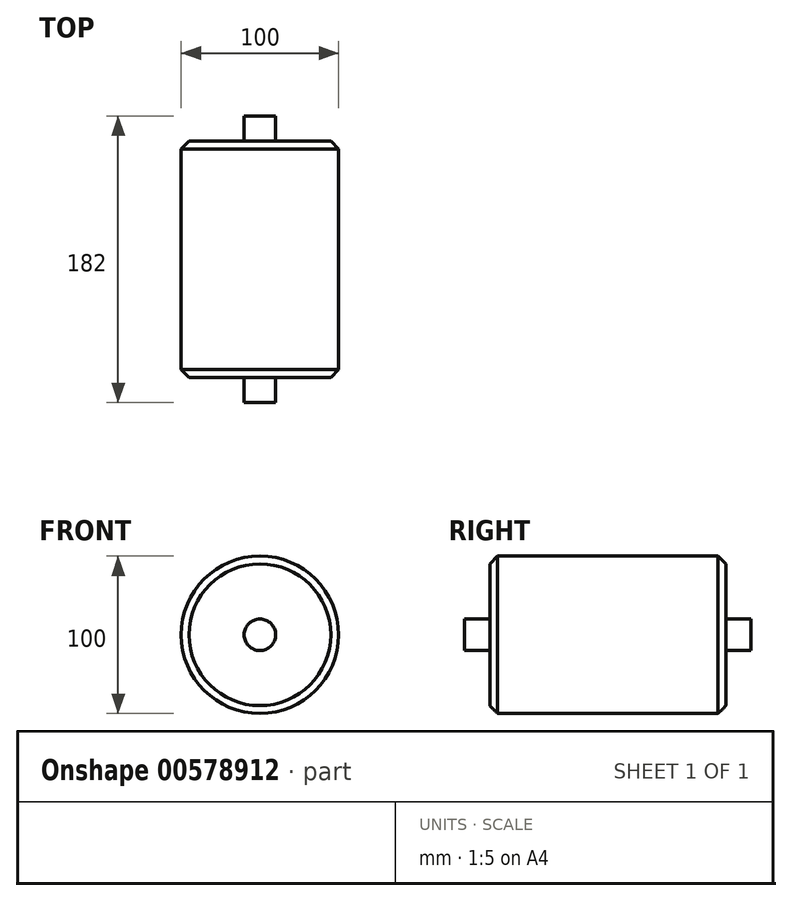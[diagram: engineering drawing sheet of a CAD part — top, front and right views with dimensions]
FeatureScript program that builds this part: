
annotation { "Feature Type Name" : "Feature", "Feature Type Description" : "" }
export const myFeature = defineFeature(function(context is Context, id is Id, definition is map)
    precondition{}
    {
        {
            var Q0;
            Q0=qCreatedBy(makeId("Front.planeOp"),FACE);
            var sketch = newSketch(context, id + "F0", { "sketchPlane" : qUnion([Q0])});
            skCircle(sketch, "E0", {"center": v(0, 0) * mm, "radius": 50 * mm});
            skSolve(sketch);
        }
        {
            var Q0;
            Q0 = qSketchRegion(id + "F0", true);
            extrude(context, id + "F1", {"entities" : qUnion([Q0]), "endBound" : BoundingType.SYMMETRIC, "depth" : 150 * mm, "offsetDistance" : 25 * mm});
        }
        {
            var Q0;
            Q0=makeQuery(id+"F1.opExtrude","CAP_FACE",FACE,{"disambiguationData":[OSD([sQuery(id+"F0.wireOp",EDGE,"E0")])],"isStart":false});
            var sketch = newSketch(context, id + "F2", { "sketchPlane" : qUnion([Q0])});
            skCircle(sketch, "E1", {"center": v(0, 0) * mm, "radius": 10 * mm});
            skSolve(sketch);
        }
        {
            var Q0;
            Q0 = qSketchRegion(id + "F2", true);
            extrude(context, id + "F3", {"entities" : qUnion([Q0]), "operationType" : NewBodyOperationType.ADD, "depth" : 16 * mm, "offsetDistance" : 25 * mm});
        }
        {
            var Q0;
            Q0=makeQuery(id+"F1.opExtrude","SWEPT_BODY",BODY,{"disambiguationData":[OSD([sQuery(id+"F0.wireOp",EDGE,"E0")])]});
            var Q1;
            Q1=qCreatedBy(makeId("Front.planeOp"),FACE);
            mirror(context, id + "F4", {"operationType" : NewBodyOperationType.ADD, "entities" : qUnion([Q0]), "mirrorPlane" : qUnion([Q1])});
        }
        {
            var Q0;
            Q0=makeQuery(id+"F1.opExtrude","CAP_EDGE",EDGE,{"disambiguationData":[OSD([sQuery(id+"F0.wireOp",EDGE,"E0")])],"isStart":true});
            var Q1;
            Q1=makeQuery(id+"F1.opExtrude","CAP_EDGE",EDGE,{"disambiguationData":[OSD([sQuery(id+"F0.wireOp",EDGE,"E0")])],"isStart":false});
            chamfer(context, id + "F5", {"entities" : qUnion([Q0, Q1]), "width" : 5 * mm, "tangentPropagation" : true});
        }
    });
